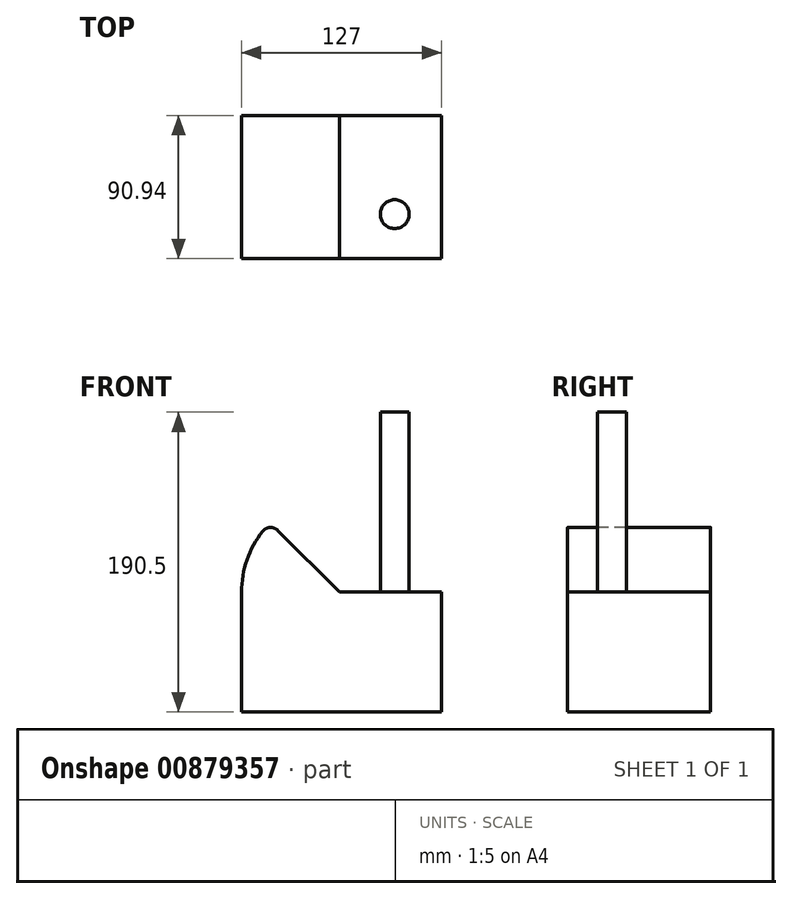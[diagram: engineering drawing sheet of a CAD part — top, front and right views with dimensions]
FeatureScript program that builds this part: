
annotation { "Feature Type Name" : "Feature", "Feature Type Description" : "" }
export const myFeature = defineFeature(function(context is Context, id is Id, definition is map)
    precondition{}
    {
        {
            var Q0;
            Q0=qCreatedBy(makeId("Top.planeOp"),FACE);
            var sketch = newSketch(context, id + "F0", { "sketchPlane" : qUnion([Q0])});
            skLineSegment(sketch, "E0.bottom", {"start": v(-62.16, 47.48) * mm, "end": v(64.84, 47.48) * mm});
            skLineSegment(sketch, "E0.top", {"start": v(-62.16, -43.46) * mm, "end": v(64.84, -43.46) * mm});
            skLineSegment(sketch, "E0.left", {"start": v(-62.16, 47.48) * mm, "end": v(-62.16, -43.46) * mm});
            skLineSegment(sketch, "E0.right", {"start": v(64.84, 47.48) * mm, "end": v(64.84, -43.46) * mm});
            skSolve(sketch);
        }
        {
            var Q0;
            Q0=makeQuery(id+"F0.imprint","IMPRINT",FACE,{"disambiguationData":[TD([[makeQuery(id+"F0.imprint","IMPRINT",EDGE,{"derivedFrom":sQuery(id+"F0.wireOp",EDGE,"E0.bottom")}),-1.0]])]});
            extrude(context, id + "F1", {"entities" : qUnion([Q0]), "depth" : 76.2 * mm, "offsetDistance" : 25.4 * mm});
        }
        {
            var Q0;
            Q0=makeQuery(id+"F1.opExtrude","CAP_FACE",FACE,{"disambiguationData":[OSD([sQuery(id+"F0.wireOp",EDGE,"E0.bottom"),sQuery(id+"F0.wireOp",EDGE,"E0.top"),sQuery(id+"F0.wireOp",EDGE,"E0.left"),sQuery(id+"F0.wireOp",EDGE,"E0.right")])],"isStart":false});
            var sketch = newSketch(context, id + "F2", { "sketchPlane" : qUnion([Q0])});
            skPoint(sketch, "E1.oppositeSnap0", {"position": v(1.34, 47.48) * mm});
            skLineSegment(sketch, "E1.bottom", {"start": v(-62.16, -43.46) * mm, "end": v(0, -43.46) * mm});
            skLineSegment(sketch, "E1.top", {"start": v(-62.16, 47.48) * mm, "end": v(0, 47.48) * mm});
            skLineSegment(sketch, "E1.left", {"start": v(-62.16, -43.46) * mm, "end": v(-62.16, 47.48) * mm});
            skLineSegment(sketch, "E1.right", {"start": v(0, -43.46) * mm, "end": v(0, 47.48) * mm});
            skSolve(sketch);
        }
        {
            var Q0;
            Q0=makeQuery(id+"F1.opExtrude","CAP_FACE",FACE,{"disambiguationData":[OSD([sQuery(id+"F0.wireOp",EDGE,"E0.bottom"),sQuery(id+"F0.wireOp",EDGE,"E0.top"),sQuery(id+"F0.wireOp",EDGE,"E0.left"),sQuery(id+"F0.wireOp",EDGE,"E0.right")])],"isStart":false});
            var sketch = newSketch(context, id + "F3", { "sketchPlane" : qUnion([Q0])});
            skSolve(sketch);
        }
        {
            var Q0;
            Q0=makeQuery(id+"F2.imprint","IMPRINT",FACE,{"disambiguationData":[TD([[makeQuery(id+"F2.imprint","IMPRINT",EDGE,{"derivedFrom":sQuery(id+"F2.wireOp",EDGE,"E1.bottom")}),1.0]])]});
            var Q1;
            Q1=sQuery(id+"F2.wireOp",EDGE,"E1.right");
            revolve(context, id + "F4", {"operationType" : NewBodyOperationType.ADD, "surfaceOperationType" : NewSurfaceOperationType.NEW, "entities" : qUnion([Q0]), "axis" : qUnion([Q1]), "revolveType" : RevolveType.ONE_DIRECTION, "angle" : 45 * degree});
        }
        {
            var Q0;
            Q0=makeQuery(id+"F3.imprint","IMPRINT",FACE,{"disambiguationData":[TD([[makeQuery(id+"F3.imprint","IMPRINT",EDGE,{"derivedFrom":makeQuery(id+"F1.opExtrude","CAP_EDGE",EDGE,{"disambiguationData":[OSD([sQuery(id+"F0.wireOp",EDGE,"E0.bottom")])],"isStart":false})}),-1.0]])]});
            var sketch = newSketch(context, id + "F5", { "sketchPlane" : qUnion([Q0])});
            skCircle(sketch, "E2", {"center": v(35.1, -15.2) * mm, "radius": 9.17 * mm});
            skSolve(sketch);
        }
        {
            var Q0;
            Q0=makeQuery(id+"F5.imprint","IMPRINT",FACE,{"disambiguationData":[TD([[makeQuery(id+"F5.imprint","IMPRINT",EDGE,{"derivedFrom":sQuery(id+"F5.wireOp",EDGE,"E2")}),1.0]])]});
            extrude(context, id + "F6", {"entities" : qUnion([Q0]), "operationType" : NewBodyOperationType.ADD, "depth" : 114.3 * mm, "offsetDistance" : 25.4 * mm});
        }
        {
            var Q0;
            Q0=makeQuery(id+"F4.opRevolve","CAP_EDGE",EDGE,{"disambiguationData":[OSD([sQuery(id+"F2.wireOp",EDGE,"E1.left")])],"isStart":false});
            fillet(context, id + "F7", {"entities" : qUnion([Q0]), "radius" : 6.35 * mm, "tangentPropagation" : true, "allowEdgeOverflow" : false});
        }
    });
